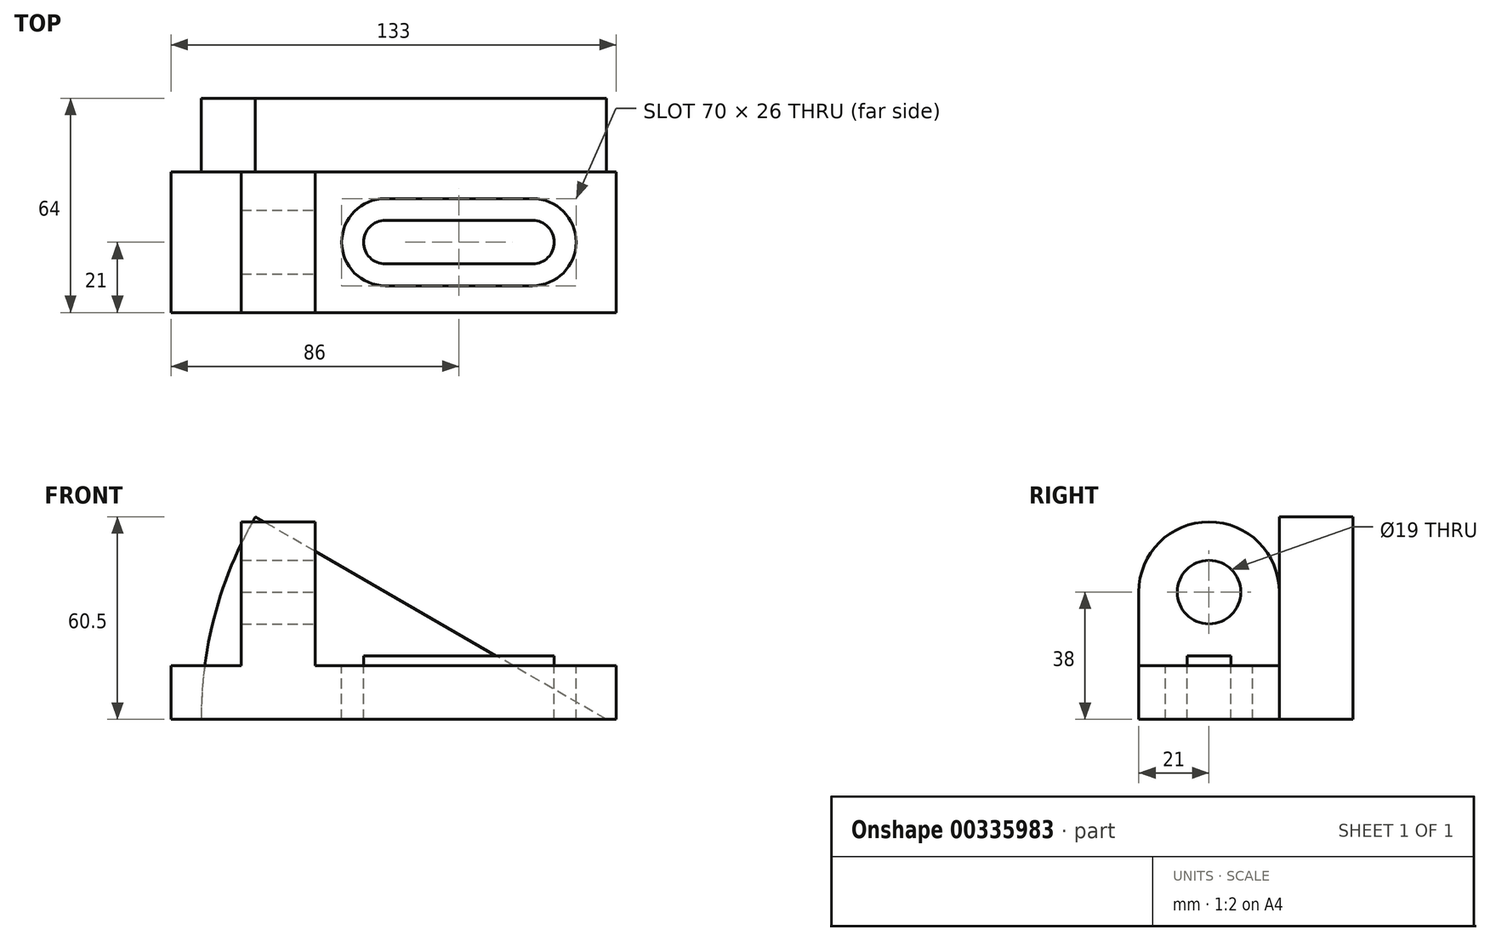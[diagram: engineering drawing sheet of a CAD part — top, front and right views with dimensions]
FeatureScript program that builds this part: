
annotation { "Feature Type Name" : "Feature", "Feature Type Description" : "" }
export const myFeature = defineFeature(function(context is Context, id is Id, definition is map)
    precondition{}
    {
        {
            var Q0;
            Q0=qCreatedBy(makeId("Front.planeOp"),FACE);
            var sketch = newSketch(context, id + "F0", { "sketchPlane" : qUnion([Q0])});
            skLineSegment(sketch, "E0.bottom", {"start": v(0, 0) * mm, "end": v(133, 0) * mm});
            skLineSegment(sketch, "E0.top", {"start": v(0, 16) * mm, "end": v(133, 16) * mm});
            skLineSegment(sketch, "E0.left", {"start": v(0, 0) * mm, "end": v(0, 16) * mm});
            skLineSegment(sketch, "E0.right", {"start": v(133, 0) * mm, "end": v(133, 16) * mm});
            skSolve(sketch);
        }
        {
            var Q0;
            Q0 = qSketchRegion(id + "F0", true);
            extrude(context, id + "F1", {"entities" : qUnion([Q0]), "depth" : 42 * mm});
        }
        {
            var Q0;
            Q0=makeQuery(id+"F1.opExtrude","SWEPT_FACE",FACE,{"disambiguationData":[OSD([sQuery(id+"F0.wireOp",EDGE,"E0.top")])]});
            var sketch = newSketch(context, id + "F2", { "sketchPlane" : qUnion([Q0])});
            skLineSegment(sketch, "E1.bottom", {"start": v(21, -42) * mm, "end": v(43, -42) * mm});
            skLineSegment(sketch, "E1.top", {"start": v(21, 0) * mm, "end": v(43, 0) * mm});
            skLineSegment(sketch, "E1.left", {"start": v(21, -42) * mm, "end": v(21, 0) * mm});
            skLineSegment(sketch, "E1.right", {"start": v(43, -42) * mm, "end": v(43, 0) * mm});
            skLineSegment(sketch, "E2", {"start": v(64, -21) * mm, "end": v(108, -21) * mm, "construction": true});
            skArc(sketch, "E3.0.startCap", {"start": v(64, -27.5) * mm, "mid": v(57.5, -21) * mm, "end": v(64, -14.5) * mm});
            skArc(sketch, "E3.0.endCap", {"start": v(108, -14.5) * mm, "mid": v(114.5, -21) * mm, "end": v(108, -27.5) * mm});
            skLineSegment(sketch, "E3.0.left", {"start": v(64, -14.5) * mm, "end": v(108, -14.5) * mm});
            skLineSegment(sketch, "E3.0.right", {"start": v(64, -27.5) * mm, "end": v(108, -27.5) * mm});
            skLineSegment(sketch, "E4.0", {"start": v(64, -34) * mm, "end": v(108, -34) * mm});
            skLineSegment(sketch, "E5.0", {"start": v(64, -8) * mm, "end": v(108, -8) * mm});
            skArc(sketch, "E6", {"start": v(64, -8) * mm, "mid": v(51, -21) * mm, "end": v(64, -34) * mm});
            skArc(sketch, "E7", {"start": v(108, -34) * mm, "mid": v(121, -21) * mm, "end": v(108, -8) * mm});
            skSolve(sketch);
        }
        {
            var Q0;
            Q0=makeQuery(id+"F2.imprint","IMPRINT",FACE,{"disambiguationData":[TD([[makeQuery(id+"F2.imprint","IMPRINT",EDGE,{"derivedFrom":sQuery(id+"F2.wireOp",EDGE,"E1.bottom")}),1.0]])]});
            extrude(context, id + "F3", {"entities" : qUnion([Q0]), "operationType" : NewBodyOperationType.ADD, "depth" : 22 * mm});
        }
        {
            var Q0;
            Q0=makeQuery(id+"F2.imprint","IMPRINT",FACE,{"disambiguationData":[TD([[makeQuery(id+"F2.imprint","IMPRINT",EDGE,{"derivedFrom":sQuery(id+"F2.wireOp",EDGE,"E3.0.startCap")}),-1.0]])]});
            extrude(context, id + "F4", {"entities" : qUnion([Q0]), "operationType" : NewBodyOperationType.REMOVE, "endBound" : BoundingType.THROUGH_ALL, "oppositeDirection" : true, "depth" : 25 * mm});
        }
        {
            var Q0;
            Q0=makeQuery(id+"F2.imprint","IMPRINT",FACE,{"disambiguationData":[TD([[makeQuery(id+"F2.imprint","IMPRINT",EDGE,{"derivedFrom":sQuery(id+"F2.wireOp",EDGE,"E3.0.startCap")}),1.0]])]});
            extrude(context, id + "F5", {"entities" : qUnion([Q0]), "operationType" : NewBodyOperationType.ADD, "depth" : 3 * mm});
        }
        {
            var Q0;
            Q0=makeQuery(id+"F3.opExtrude","SWEPT_FACE",FACE,{"disambiguationData":[OSD([sQuery(id+"F2.wireOp",EDGE,"E1.right")])]});
            var sketch = newSketch(context, id + "F6", { "sketchPlane" : qUnion([Q0])});
            skArc(sketch, "E8", {"start": v(0, 38) * mm, "mid": v(-21, 59) * mm, "end": v(-42, 38) * mm});
            skCircle(sketch, "E9", {"center": v(-21, 38) * mm, "radius": 9.5 * mm});
            skSolve(sketch);
        }
        {
            var Q0;
            Q0 = qSketchRegion(id + "F6", true);
            var Q1;
            Q1=makeQuery(id+"F6.imprint","IMPRINT",FACE,{"disambiguationData":[TD([[makeQuery(id+"F6.imprint","IMPRINT",EDGE,{"derivedFrom":sQuery(id+"F6.wireOp",EDGE,"E8")}),1.0]])]});
            extrude(context, id + "F7", {"entities" : qUnion([Q0, Q1]), "operationType" : NewBodyOperationType.ADD, "oppositeDirection" : true, "depth" : 22 * mm});
        }
        {
            var Q0;
            Q0 = qSketchRegion(id + "F6", true);
            extrude(context, id + "F8", {"entities" : qUnion([Q0]), "operationType" : NewBodyOperationType.REMOVE, "endBound" : BoundingType.THROUGH_ALL, "oppositeDirection" : true, "depth" : 25 * mm});
        }
        {
            var Q0;
            Q0=qCreatedBy(makeId("Front.planeOp"),FACE);
            var sketch = newSketch(context, id + "F9", { "sketchPlane" : qUnion([Q0])});
            skLineSegment(sketch, "E10.0", {"start": v(0, 0) * mm, "end": v(133, 0) * mm});
            skLineSegment(sketch, "E11", {"start": v(133, 0) * mm, "end": v(130, 0) * mm});
            skArc(sketch, "E12", {"start": v(9, 0) * mm, "mid": v(13.12, 31.32) * mm, "end": v(25.21, 60.5) * mm});
            skLineSegment(sketch, "E13", {"start": v(130, 0) * mm, "end": v(25.21, 60.5) * mm});
            skSolve(sketch);
        }
        {
            var Q0;
            Q0 = qSketchRegion(id + "F9", true);
            extrude(context, id + "F10", {"entities" : qUnion([Q0]), "operationType" : NewBodyOperationType.ADD, "oppositeDirection" : true, "depth" : 22 * mm});
        }
    });
